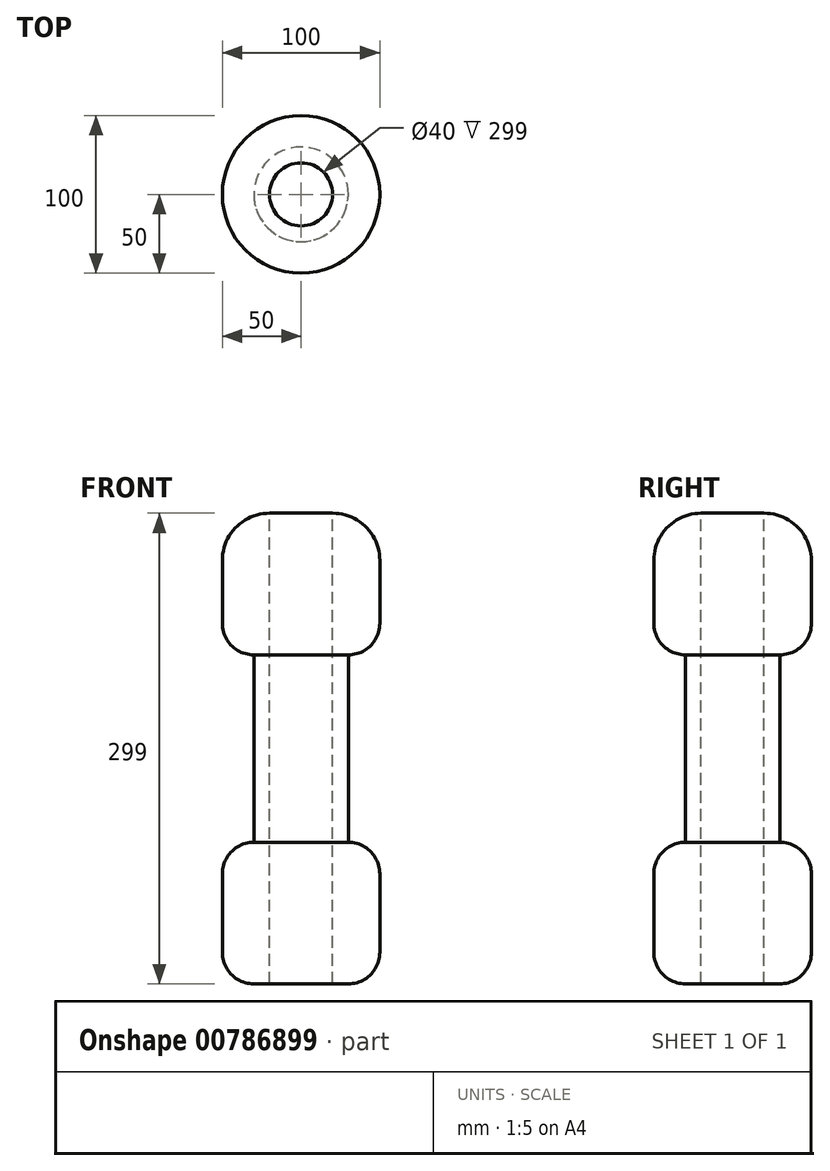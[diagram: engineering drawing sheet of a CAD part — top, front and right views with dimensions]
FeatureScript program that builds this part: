
annotation { "Feature Type Name" : "Feature", "Feature Type Description" : "" }
export const myFeature = defineFeature(function(context is Context, id is Id, definition is map)
    precondition{}
    {
        {
            var Q0;
            Q0=qCreatedBy(makeId("Top.planeOp"),FACE);
            var sketch = newSketch(context, id + "F0", { "sketchPlane" : qUnion([Q0])});
            skCircle(sketch, "E0", {"center": v(0, 0) * mm, "radius": 50 * mm});
            skSolve(sketch);
        }
        {
            var Q0;
            Q0=makeQuery(id+"F0.imprint","IMPRINT",FACE,{"disambiguationData":[TD([[makeQuery(id+"F0.imprint","IMPRINT",EDGE,{"derivedFrom":sQuery(id+"F0.wireOp",EDGE,"E0")}),1.0]])]});
            extrude(context, id + "F1", {"entities" : qUnion([Q0]), "depth" : 45 * mm, "offsetDistance" : 25 * mm});
        }
        {
            var Q0;
            Q0=makeQuery(id+"F1.opExtrude","CAP_EDGE",EDGE,{"disambiguationData":[OSD([sQuery(id+"F0.wireOp",EDGE,"E0")])],"isStart":false});
            fillet(context, id + "F2", {"entities" : qUnion([Q0]), "radius" : 30 * mm, "tangentPropagation" : true, "allowEdgeOverflow" : false});
        }
        {
            var Q0;
            Q0=makeQuery(id+"F1.opExtrude","CAP_FACE",FACE,{"disambiguationData":[OSD([sQuery(id+"F0.wireOp",EDGE,"E0")])],"isStart":false});
            extrude(context, id + "F3", {"entities" : qUnion([Q0]), "operationType" : NewBodyOperationType.REMOVE, "oppositeDirection" : true, "depth" : 144 * mm, "offsetDistance" : 25 * mm});
        }
        {
            var Q0;
            Q0=makeQuery(id+"F1.opExtrude","CAP_FACE",FACE,{"disambiguationData":[OSD([sQuery(id+"F0.wireOp",EDGE,"E0")])],"isStart":true});
            extrude(context, id + "F4", {"entities" : qUnion([Q0]), "operationType" : NewBodyOperationType.ADD, "depth" : 45 * mm, "offsetDistance" : 25 * mm});
        }
        {
            var Q0;
            {var subQ0=sQuery(id+"F0.wireOp",EDGE,"E0");Q0=makeQuery(id+"F4.boolean.opBoolean","MERGE",FACE,{"derivedFrom":[makeQuery(id+"F1.opExtrude","SWEPT_FACE",FACE,{"disambiguationData":[OSD([subQ0])]}),makeQuery(id+"F4.opExtrude","SWEPT_FACE",FACE,{"disambiguationData":[OSD([subQ0]),TDD([makeQuery(id+"F1.opExtrude","CAP_EDGE",EDGE,{"disambiguationData":[OSD([subQ0])],"isStart":true})])]})]});}
            fillet(context, id + "F5", {"entities" : qUnion([Q0]), "radius" : 20 * mm, "tangentPropagation" : true, "allowEdgeOverflow" : false});
        }
        {
            var Q0;
            Q0=makeQuery(id+"F4.opExtrude","CAP_FACE",FACE,{"disambiguationData":[OSD([sQuery(id+"F0.wireOp",EDGE,"E0")])],"isStart":false});
            var sketch = newSketch(context, id + "F6", { "sketchPlane" : qUnion([Q0])});
            skSolve(sketch);
        }
        {
            var Q0;
            Q0 = qSketchRegion(id + "F6", true);
            var Q1;
            {var subQ0=sQuery(id+"F0.wireOp",EDGE,"E0");Q1=makeQuery(id+"F6.imprint","IMPRINT",FACE,{"disambiguationData":[TD([[makeQuery(id+"F6.imprint","IMPRINT",EDGE,{"derivedFrom":makeQuery(id+"F4.opExtrude","CAP_EDGE",EDGE,{"disambiguationData":[OSD([subQ0]),TDD([makeQuery(id+"F3.boolean.opBoolean","INTERSECT",EDGE,{"derivedFrom":[makeQuery(id+"F1.opExtrude","CAP_FACE",FACE,{"disambiguationData":[OSD([subQ0])],"isStart":true}),makeQuery(id+"F3.opExtrude","SWEPT_FACE",FACE,{"disambiguationData":[OSD([subQ0])]})]})])],"isStart":false})}),1.0]])]});}
            extrude(context, id + "F7", {"entities" : qUnion([Q0, Q1]), "operationType" : NewBodyOperationType.ADD, "depth" : 25 * mm, "offsetDistance" : 25 * mm});
        }
        {
            var Q0;
            Q0=makeQuery(id+"F7.opExtrude","CAP_FACE",FACE,{"disambiguationData":[OSD([sQuery(id+"F0.wireOp",EDGE,"E0")])],"isStart":false});
            extrude(context, id + "F8", {"entities" : qUnion([Q0]), "operationType" : NewBodyOperationType.ADD, "depth" : 25 * mm, "offsetDistance" : 25 * mm});
        }
        {
            var Q0;
            Q0=makeQuery(id+"F8.opExtrude","CAP_FACE",FACE,{"disambiguationData":[OSD([sQuery(id+"F0.wireOp",EDGE,"E0")])],"isStart":false});
            extrude(context, id + "F9", {"entities" : qUnion([Q0]), "operationType" : NewBodyOperationType.ADD, "depth" : 69 * mm, "offsetDistance" : 25 * mm});
        }
        {
            var Q0;
            Q0=makeQuery(id+"F9.opExtrude","CAP_FACE",FACE,{"disambiguationData":[OSD([sQuery(id+"F0.wireOp",EDGE,"E0")])],"isStart":false});
            var sketch = newSketch(context, id + "F10", { "sketchPlane" : qUnion([Q0])});
            skCircle(sketch, "E1", {"center": v(0, 0) * mm, "radius": 50 * mm});
            skSolve(sketch);
        }
        {
            var Q0;
            Q0 = qSketchRegion(id + "F10", true);
            extrude(context, id + "F11", {"entities" : qUnion([Q0]), "operationType" : NewBodyOperationType.ADD, "depth" : 45 * mm, "offsetDistance" : 25 * mm});
        }
        {
            var Q0;
            Q0=makeQuery(id+"F11.opExtrude","CAP_FACE",FACE,{"disambiguationData":[OSD([sQuery(id+"F10.wireOp",EDGE,"E1")])],"isStart":false});
            extrude(context, id + "F12", {"entities" : qUnion([Q0]), "operationType" : NewBodyOperationType.ADD, "depth" : 45 * mm, "offsetDistance" : 25 * mm});
        }
        {
            var Q0;
            {var subQ0=sQuery(id+"F10.wireOp",EDGE,"E1");Q0=makeQuery(id+"F12.boolean.opBoolean","MERGE",FACE,{"derivedFrom":[makeQuery(id+"F11.opExtrude","SWEPT_FACE",FACE,{"disambiguationData":[OSD([subQ0])]}),makeQuery(id+"F12.opExtrude","SWEPT_FACE",FACE,{"disambiguationData":[OSD([subQ0])]})]});}
            fillet(context, id + "F13", {"entities" : qUnion([Q0]), "radius" : 20 * mm, "tangentPropagation" : true, "allowEdgeOverflow" : false});
        }
        {
            var Q0;
            {var subQ0=sQuery(id+"F0.wireOp",EDGE,"E0");var subQ1=makeQuery(id+"F3.opExtrude","SWEPT_FACE",FACE,{"disambiguationData":[OSD([subQ0])]});Q0=makeQuery(id+"F11.boolean.opBoolean","SPLIT",FACE,{"disambiguationData":[TD([makeQuery(id+"F3.boolean.opBoolean","COPY",FACE,{"derivedFrom":subQ1})])],"derivedFrom":makeQuery(id+"F11.opExtrude","CAP_FACE",FACE,{"disambiguationData":[OSD([sQuery(id+"F10.wireOp",EDGE,"E1")])],"isStart":true})});}
            extrude(context, id + "F14", {"entities" : qUnion([Q0]), "operationType" : NewBodyOperationType.REMOVE, "oppositeDirection" : true, "depth" : 491 * mm, "offsetDistance" : 25 * mm});
        }
    });
